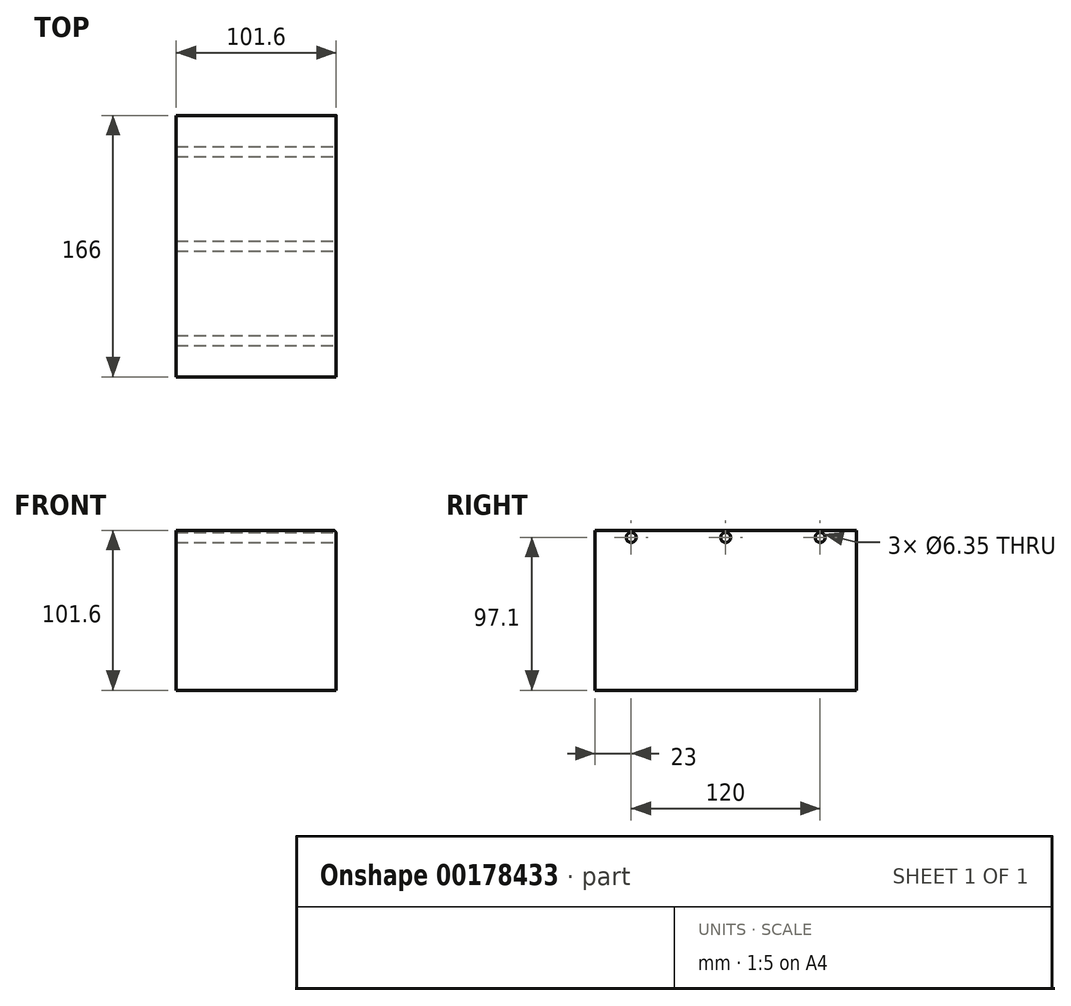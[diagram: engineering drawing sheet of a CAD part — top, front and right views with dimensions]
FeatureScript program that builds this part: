
annotation { "Feature Type Name" : "Feature", "Feature Type Description" : "" }
export const myFeature = defineFeature(function(context is Context, id is Id, definition is map)
    precondition{}
    {
        {
            var Q0;
            Q0=qCreatedBy(makeId("Front.planeOp"),FACE);
            var sketch = newSketch(context, id + "F0", { "sketchPlane" : qUnion([Q0])});
            skLineSegment(sketch, "E0.bottom", {"start": v(50.8, 50.8) * mm, "end": v(-50.8, 50.8) * mm});
            skLineSegment(sketch, "E0.top", {"start": v(50.8, -50.8) * mm, "end": v(-50.8, -50.8) * mm});
            skLineSegment(sketch, "E0.left", {"start": v(50.8, 50.8) * mm, "end": v(50.8, -50.8) * mm});
            skLineSegment(sketch, "E0.right", {"start": v(-50.8, 50.8) * mm, "end": v(-50.8, -50.8) * mm});
            skPoint(sketch, "E0.middle", {"position": v(0, 0) * mm});
            skSolve(sketch);
        }
        {
            var Q0;
            Q0=makeQuery(id+"F0.imprint","IMPRINT",FACE,{"disambiguationData":[TD([[makeQuery(id+"F0.imprint","IMPRINT",EDGE,{"derivedFrom":sQuery(id+"F0.wireOp",EDGE,"E0.bottom")}),1.0]])]});
            extrude(context, id + "F1", {"entities" : qUnion([Q0]), "depth" : 166 * mm});
        }
        {
            var Q0;
            Q0=makeQuery(id+"F1.opExtrude","SWEPT_FACE",FACE,{"disambiguationData":[OSD([sQuery(id+"F0.wireOp",EDGE,"E0.left")])]});
            var sketch = newSketch(context, id + "F2", { "sketchPlane" : qUnion([Q0])});
            skPoint(sketch, "E1", {"position": v(-143, 46.3) * mm});
            skPoint(sketch, "E2", {"position": v(-83, 46.3) * mm});
            skPoint(sketch, "E3", {"position": v(-23, 46.3) * mm});
            skLineSegment(sketch, "E4.0.0", {"start": v(0, -50.8) * mm, "end": v(0, 50.8) * mm});
            skLineSegment(sketch, "E4.0.1", {"start": v(0, 50.8) * mm, "end": v(-166, 50.8) * mm});
            skLineSegment(sketch, "E4.0.2", {"start": v(-166, 50.8) * mm, "end": v(-166, -50.8) * mm});
            skLineSegment(sketch, "E4.0.3", {"start": v(-166, -50.8) * mm, "end": v(0, -50.8) * mm});
            skLineSegment(sketch, "E5", {"start": v(-166, 41.8) * mm, "end": v(0, 41.8) * mm});
            skCircle(sketch, "E6", {"center": v(-143, 46.3) * mm, "radius": 3.18 * mm});
            skCircle(sketch, "E7", {"center": v(-83, 46.3) * mm, "radius": 3.18 * mm});
            skCircle(sketch, "E8", {"center": v(-23, 46.3) * mm, "radius": 3.18 * mm});
            skSolve(sketch);
        }
        {
            var Q0;
            Q0=makeQuery(id+"F2.imprint","IMPRINT",FACE,{"disambiguationData":[TD([[makeQuery(id+"F2.imprint","IMPRINT",EDGE,{"derivedFrom":sQuery(id+"F2.wireOp",EDGE,"E6")}),1.0]])]});
            var Q1;
            Q1=makeQuery(id+"F2.imprint","IMPRINT",FACE,{"disambiguationData":[TD([[makeQuery(id+"F2.imprint","IMPRINT",EDGE,{"derivedFrom":sQuery(id+"F2.wireOp",EDGE,"E7")}),1.0]])]});
            var Q2;
            Q2=makeQuery(id+"F2.imprint","IMPRINT",FACE,{"disambiguationData":[TD([[makeQuery(id+"F2.imprint","IMPRINT",EDGE,{"derivedFrom":sQuery(id+"F2.wireOp",EDGE,"E8")}),1.0]])]});
            extrude(context, id + "F3", {"entities" : qUnion([Q0, Q1, Q2]), "operationType" : NewBodyOperationType.REMOVE, "endBound" : BoundingType.THROUGH_ALL, "oppositeDirection" : true, "depth" : 25 * mm});
        }
        {
            var Q0;
            Q0=makeQuery(id+"F1.opExtrude","SWEPT_EDGE",EDGE,{"disambiguationData":[OSD([sQuery(id+"F0.wireOp",EDGE,"E0.bottom"),sQuery(id+"F0.wireOp",EDGE,"E0.left")])]});
            fillet(context, id + "F4", {"entities" : qUnion([Q0]), "radius" : 2 * mm, "tangentPropagation" : true, "allowEdgeOverflow" : false});
        }
    });
